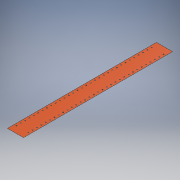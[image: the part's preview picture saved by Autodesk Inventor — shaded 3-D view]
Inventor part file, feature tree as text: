
AUTODESK INVENTOR PART (.ipt)
format: ipt  version: 2019 (Build 230136000, 136)  size: 231,424 bytes
history: native  units: mm
features: extrude x2, other x2, mirror x1
ambient origin geometry x8: Origin, YZ Plane, XZ Plane, XY Plane, X Axis, Y Axis, Z Axis, Center Point
bodies: Body1 (feature_tree)
feature tree (5):
  extrude  "Skin Body"  Depth=1670.0mm
  extrude  "End Cut"  Depth=835.0mm
  mirror  "End Cut Mirror"
  other  "Skin Scheme"
  other  "End Cut Outline"
